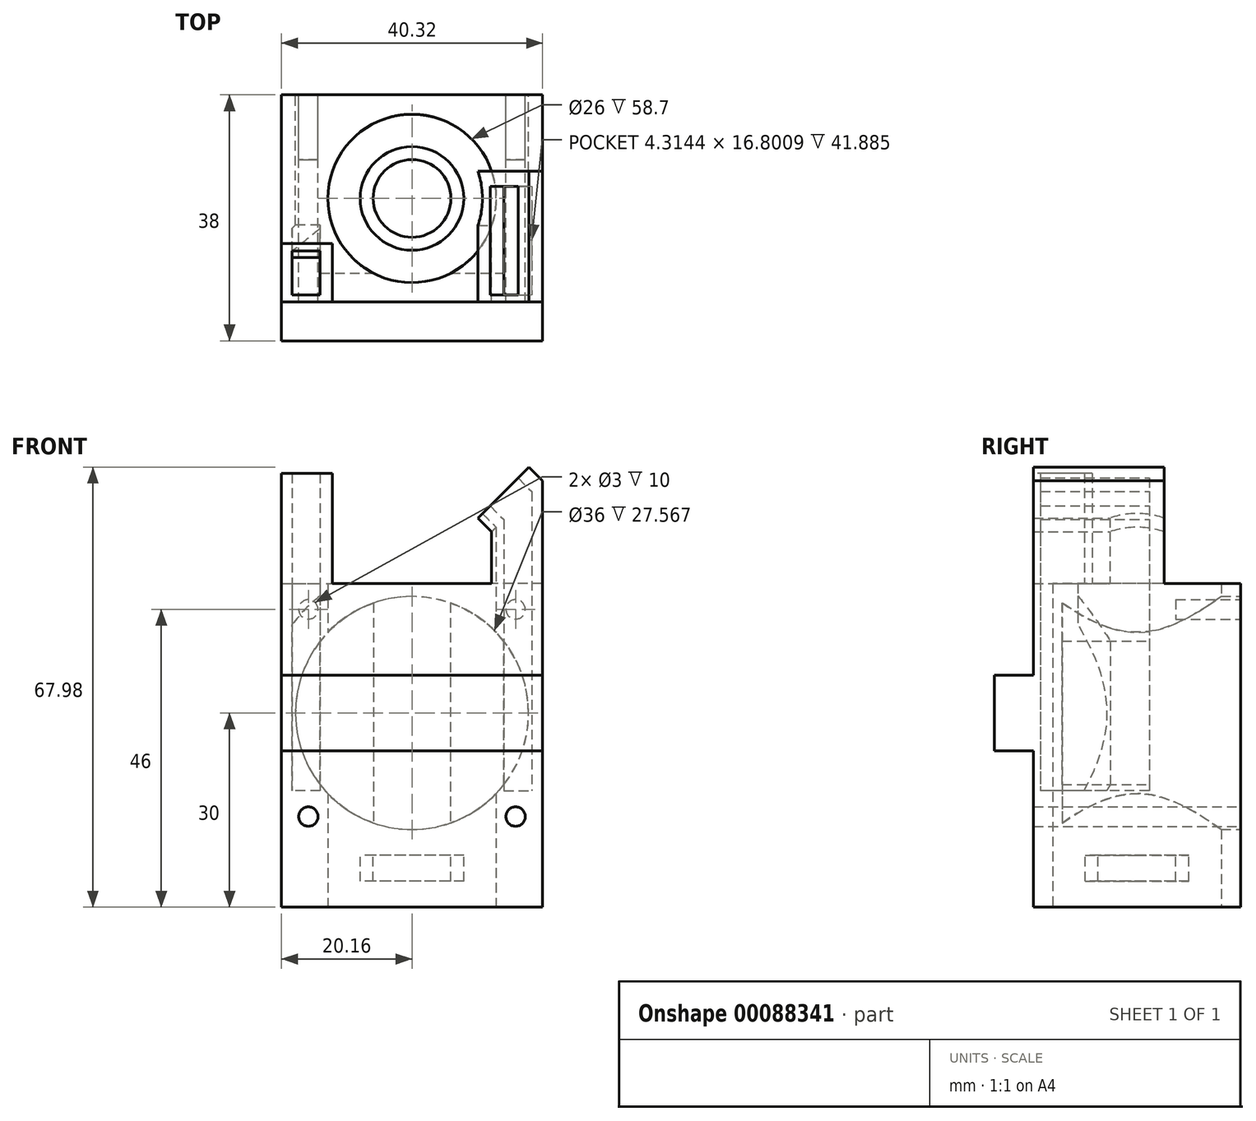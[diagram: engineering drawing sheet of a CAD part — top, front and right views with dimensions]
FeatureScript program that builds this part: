
annotation { "Feature Type Name" : "Feature", "Feature Type Description" : "" }
export const myFeature = defineFeature(function(context is Context, id is Id, definition is map)
    precondition{}
    {
        {
            var Q0;
            Q0=qCreatedBy(makeId("Top.planeOp"),FACE);
            var sketch = newSketch(context, id + "F16", { "sketchPlane" : qUnion([Q0])});
            skCircle(sketch, "E0", {"center": v(0, 0) * mm, "radius": 8 * mm});
            skCircle(sketch, "E1.cCircle", {"center": v(0, 0) * mm, "radius": 13 * mm, "construction": true});
            skLineSegment(sketch, "E1.0", {"start": v(13, 13) * mm, "end": v(13, -13) * mm});
            skLineSegment(sketch, "E1.1", {"start": v(13, -13) * mm, "end": v(-13, -13) * mm});
            skLineSegment(sketch, "E1.2", {"start": v(-13, -13) * mm, "end": v(-13, 13) * mm});
            skLineSegment(sketch, "E1.3", {"start": v(-13, 13) * mm, "end": v(13, 13) * mm});
            skPoint(sketch, "E1.0.midPoint", {"position": v(13, 0) * mm});
            skLineSegment(sketch, "E2", {"start": v(0, 0) * mm, "end": v(8, 0) * mm, "construction": true});
            skPoint(sketch, "E3.0.midPoint", {"position": v(0, 36.09) * mm});
            skLineSegment(sketch, "E4", {"start": v(0, 0) * mm, "end": v(0, -16) * mm, "construction": true});
            skPoint(sketch, "E5", {"position": v(0, -13) * mm});
            skLineSegment(sketch, "E6", {"start": v(0, -16) * mm, "end": v(20.16, -16) * mm});
            skLineSegment(sketch, "E7", {"start": v(20.16, -16) * mm, "end": v(20.16, 0) * mm});
            skLineSegment(sketch, "E8.MirrorCS", {"start": v(0, 16) * mm, "end": v(20.16, 16) * mm});
            skLineSegment(sketch, "E9.MirrorCS", {"start": v(20.16, 16) * mm, "end": v(20.16, 0) * mm});
            skLineSegment(sketch, "E10.MirrorCS", {"start": v(0, 16) * mm, "end": v(-20.16, 16) * mm});
            skLineSegment(sketch, "E11.MirrorCS", {"start": v(-20.16, 16) * mm, "end": v(-20.16, 0) * mm});
            skLineSegment(sketch, "E12.MirrorCS", {"start": v(0, -16) * mm, "end": v(-20.16, -16) * mm});
            skLineSegment(sketch, "E13.trimOffspring", {"start": v(13, 0) * mm, "end": v(20.16, 0) * mm, "construction": true});
            skPoint(sketch, "E14.middle", {"position": v(16.58, 0) * mm});
            skCircle(sketch, "E15", {"center": v(0, 0) * mm, "radius": 6 * mm});
            skCircle(sketch, "E16", {"center": v(0, 0) * mm, "radius": 13 * mm});
            skLineSegment(sketch, "E17.bottom", {"start": v(14.19, 1.9) * mm, "end": v(18.5, 1.9) * mm});
            skLineSegment(sketch, "E17.top", {"start": v(14.19, -14.9) * mm, "end": v(18.5, -14.9) * mm});
            skLineSegment(sketch, "E17.left", {"start": v(14.19, 1.9) * mm, "end": v(14.19, -14.9) * mm});
            skLineSegment(sketch, "E17.right", {"start": v(18.5, 1.9) * mm, "end": v(18.5, -14.9) * mm});
            skLineSegment(sketch, "E18.MirrorCS", {"start": v(-14.19, -14.9) * mm, "end": v(-18.5, -14.9) * mm});
            skLineSegment(sketch, "E19.MirrorCS", {"start": v(-18.5, 1.9) * mm, "end": v(-18.5, -14.9) * mm});
            skLineSegment(sketch, "E20.MirrorCS", {"start": v(-14.19, 1.9) * mm, "end": v(-18.5, 1.9) * mm});
            skLineSegment(sketch, "E21.MirrorCS", {"start": v(-14.19, 1.9) * mm, "end": v(-14.19, -14.9) * mm});
            skCircle(sketch, "E22.cCircle", {"center": v(0, 0) * mm, "radius": 12.5 * mm, "construction": true});
            skLineSegment(sketch, "E22.0", {"start": v(21.65, -12.5) * mm, "end": v(-21.65, -12.5) * mm, "construction": true});
            skPoint(sketch, "E22.0.midPoint", {"position": v(0, -12.5) * mm});
            skCircle(sketch, "E23.cCircle", {"center": v(0, 0) * mm, "radius": 9.5 * mm, "construction": true});
            skLineSegment(sketch, "E23.0", {"start": v(-16.45, 9.5) * mm, "end": v(16.45, 9.5) * mm, "construction": true});
            skLineSegment(sketch, "E23.1", {"start": v(16.45, 9.5) * mm, "end": v(0, -19) * mm, "construction": true});
            skLineSegment(sketch, "E23.2", {"start": v(0, -19) * mm, "end": v(-16.45, 9.5) * mm, "construction": true});
            skPoint(sketch, "E23.0.midPoint", {"position": v(0, 9.5) * mm});
            skCircle(sketch, "E24", {"center": v(-16.45, 9.5) * mm, "radius": 1.5 * mm});
            skCircle(sketch, "E25", {"center": v(16.45, 9.5) * mm, "radius": 1.5 * mm});
            skCircle(sketch, "E26", {"center": v(0, -19) * mm, "radius": 1.5 * mm});
            skArc(sketch, "E27", {"start": v(-13, -16) * mm, "mid": v(0, -22.28) * mm, "end": v(13, -16) * mm});
            skPoint(sketch, "E27.endSnap0", {"position": v(10.08, -16) * mm});
            skLineSegment(sketch, "E28.bottom", {"start": v(-20.16, -16) * mm, "end": v(-24.56, -16) * mm});
            skLineSegment(sketch, "E28.top", {"start": v(-20.16, 0) * mm, "end": v(-24.56, 0) * mm});
            skLineSegment(sketch, "E28.right", {"start": v(-25.56, -15) * mm, "end": v(-25.56, -1) * mm});
            skLineSegment(sketch, "E29.0", {"start": v(-20.16, -1.4) * mm, "end": v(-24.16, -1.4) * mm});
            skLineSegment(sketch, "E29.2", {"start": v(-20.16, -14.6) * mm, "end": v(-24.16, -14.6) * mm});
            skLineSegment(sketch, "E29.3", {"start": v(-24.16, -14.6) * mm, "end": v(-24.16, -1.4) * mm});
            skPoint(sketch, "E30.orphan", {"position": v(-20.16, 0) * mm});
            skLineSegment(sketch, "E31", {"start": v(-20.16, 0) * mm, "end": v(-20.16, -16) * mm});
            skPoint(sketch, "E32.visualSharp", {"position": v(-25.56, -16) * mm});
            skArc(sketch, "E32.filletArc", {"start": v(-25.56, -15) * mm, "mid": v(-25.27, -15.7) * mm, "end": v(-24.56, -16) * mm});
            skPoint(sketch, "E33.visualSharp", {"position": v(-25.56, 0) * mm});
            skArc(sketch, "E33.filletArc", {"start": v(-24.56, 0) * mm, "mid": v(-25.27, -0.3) * mm, "end": v(-25.56, -1) * mm});
            skLineSegment(sketch, "E34.MirrorCS", {"start": v(20.16, -14.6) * mm, "end": v(24.16, -14.6) * mm});
            skLineSegment(sketch, "E35.MirrorCS", {"start": v(20.16, -16) * mm, "end": v(24.56, -16) * mm});
            skLineSegment(sketch, "E36.MirrorCS", {"start": v(24.16, -14.6) * mm, "end": v(24.16, -1.4) * mm});
            skLineSegment(sketch, "E37.MirrorCS", {"start": v(25.56, -15) * mm, "end": v(25.56, -1) * mm});
            skArc(sketch, "E38.MirrorCS", {"start": v(25.56, -15) * mm, "mid": v(25.27, -15.7) * mm, "end": v(24.56, -16) * mm});
            skArc(sketch, "E39.MirrorCS", {"start": v(24.56, 0) * mm, "mid": v(25.27, -0.3) * mm, "end": v(25.56, -1) * mm});
            skLineSegment(sketch, "E40.MirrorCS", {"start": v(20.16, 0) * mm, "end": v(24.56, 0) * mm});
            skLineSegment(sketch, "E41.MirrorCS", {"start": v(20.16, -1.4) * mm, "end": v(24.16, -1.4) * mm});
            skSolve(sketch);
        }
        {
            var Q0;
            {var subQ0=sQuery(id+"F16.wireOp",EDGE,"E1.2");var subQ1=sQuery(id+"F16.wireOp",EDGE,"E1.1");var subQ2=makeQuery(id+"F16.imprint","INTERSECT",VERTEX,{"derivedFrom":[subQ1,subQ0]});Q0=makeQuery(id+"F16.imprint","IMPRINT",FACE,{"disambiguationData":[TD([[makeQuery(id+"F16.imprint","IMPRINT",EDGE,{"disambiguationData":[TD([[subQ2,1.0]])],"derivedFrom":subQ1}),-1.0]])]});}
            var Q1;
            {var subQ0=sQuery(id+"F16.wireOp",EDGE,"E1.3");var subQ1=sQuery(id+"F16.wireOp",EDGE,"E1.2");var subQ2=makeQuery(id+"F16.imprint","INTERSECT",VERTEX,{"derivedFrom":[subQ1,subQ0]});Q1=makeQuery(id+"F16.imprint","IMPRINT",FACE,{"disambiguationData":[TD([[makeQuery(id+"F16.imprint","IMPRINT",EDGE,{"disambiguationData":[TD([[subQ2,1.0]])],"derivedFrom":subQ1}),-1.0]])]});}
            var Q2;
            Q2=makeQuery(id+"F16.imprint","IMPRINT",FACE,{"disambiguationData":[TD([[makeQuery(id+"F16.imprint","IMPRINT",EDGE,{"derivedFrom":sQuery(id+"F16.wireOp",EDGE,"E6")}),1.0]])]});
            var Q3;
            {var subQ0=sQuery(id+"F16.wireOp",EDGE,"E1.1");var subQ1=sQuery(id+"F16.wireOp",EDGE,"E1.0");var subQ2=makeQuery(id+"F16.imprint","INTERSECT",VERTEX,{"derivedFrom":[subQ1,subQ0]});Q3=makeQuery(id+"F16.imprint","IMPRINT",FACE,{"disambiguationData":[TD([[makeQuery(id+"F16.imprint","IMPRINT",EDGE,{"disambiguationData":[TD([[subQ2,1.0]])],"derivedFrom":subQ1}),-1.0]])]});}
            var Q4;
            {var subQ0=sQuery(id+"F16.wireOp",EDGE,"E1.3");var subQ1=sQuery(id+"F16.wireOp",EDGE,"E1.0");var subQ2=makeQuery(id+"F16.imprint","INTERSECT",VERTEX,{"derivedFrom":[subQ1,subQ0]});Q4=makeQuery(id+"F16.imprint","IMPRINT",FACE,{"disambiguationData":[TD([[makeQuery(id+"F16.imprint","IMPRINT",EDGE,{"disambiguationData":[TD([[subQ2,-1.0]])],"derivedFrom":subQ1}),-1.0]])]});}
            var Q5;
            Q5=makeQuery(id+"F16.imprint","IMPRINT",FACE,{"disambiguationData":[TD([[makeQuery(id+"F16.imprint","IMPRINT",EDGE,{"derivedFrom":sQuery(id+"F16.wireOp",EDGE,"E24")}),1.0]])]});
            var Q6;
            Q6=makeQuery(id+"F16.imprint","IMPRINT",FACE,{"disambiguationData":[TD([[makeQuery(id+"F16.imprint","IMPRINT",EDGE,{"derivedFrom":sQuery(id+"F16.wireOp",EDGE,"E25")}),1.0]])]});
            extrude(context, id + "F0", {"entities" : qUnion([Q0, Q1, Q2, Q3, Q4, Q5, Q6]), "depth" : 32 * mm});
        }
        {
            var Q0;
            Q0=makeQuery(id+"F16.imprint","IMPRINT",FACE,{"disambiguationData":[TD([[makeQuery(id+"F16.imprint","IMPRINT",EDGE,{"derivedFrom":sQuery(id+"F16.wireOp",EDGE,"E6")}),1.0]])]});
            var Q1;
            {var subQ0=sQuery(id+"F16.wireOp",EDGE,"E1.2");var subQ1=sQuery(id+"F16.wireOp",EDGE,"E1.1");var subQ2=makeQuery(id+"F16.imprint","INTERSECT",VERTEX,{"derivedFrom":[subQ1,subQ0]});Q1=makeQuery(id+"F16.imprint","IMPRINT",FACE,{"disambiguationData":[TD([[makeQuery(id+"F16.imprint","IMPRINT",EDGE,{"disambiguationData":[TD([[subQ2,1.0]])],"derivedFrom":subQ1}),-1.0]])]});}
            var Q2;
            {var subQ0=sQuery(id+"F16.wireOp",EDGE,"E1.3");var subQ1=sQuery(id+"F16.wireOp",EDGE,"E1.2");var subQ2=makeQuery(id+"F16.imprint","INTERSECT",VERTEX,{"derivedFrom":[subQ1,subQ0]});Q2=makeQuery(id+"F16.imprint","IMPRINT",FACE,{"disambiguationData":[TD([[makeQuery(id+"F16.imprint","IMPRINT",EDGE,{"disambiguationData":[TD([[subQ2,1.0]])],"derivedFrom":subQ1}),-1.0]])]});}
            var Q3;
            {var subQ0=sQuery(id+"F16.wireOp",EDGE,"E1.3");var subQ1=sQuery(id+"F16.wireOp",EDGE,"E1.0");var subQ2=makeQuery(id+"F16.imprint","INTERSECT",VERTEX,{"derivedFrom":[subQ1,subQ0]});Q3=makeQuery(id+"F16.imprint","IMPRINT",FACE,{"disambiguationData":[TD([[makeQuery(id+"F16.imprint","IMPRINT",EDGE,{"disambiguationData":[TD([[subQ2,-1.0]])],"derivedFrom":subQ1}),-1.0]])]});}
            var Q4;
            {var subQ0=sQuery(id+"F16.wireOp",EDGE,"E1.1");var subQ1=sQuery(id+"F16.wireOp",EDGE,"E1.0");var subQ2=makeQuery(id+"F16.imprint","INTERSECT",VERTEX,{"derivedFrom":[subQ1,subQ0]});Q4=makeQuery(id+"F16.imprint","IMPRINT",FACE,{"disambiguationData":[TD([[makeQuery(id+"F16.imprint","IMPRINT",EDGE,{"disambiguationData":[TD([[subQ2,1.0]])],"derivedFrom":subQ1}),-1.0]])]});}
            var Q5;
            Q5=makeQuery(id+"F16.imprint","IMPRINT",FACE,{"disambiguationData":[TD([[makeQuery(id+"F16.imprint","IMPRINT",EDGE,{"derivedFrom":sQuery(id+"F16.wireOp",EDGE,"E14.bottom")}),-1.0]])]});
            var Q6;
            Q6=makeQuery(id+"F16.imprint","IMPRINT",FACE,{"disambiguationData":[TD([[makeQuery(id+"F16.imprint","IMPRINT",EDGE,{"derivedFrom":sQuery(id+"F16.wireOp",EDGE,"E18.MirrorCS")}),-1.0]])]});
            var Q7;
            Q7=makeQuery(id+"F16.imprint","IMPRINT",FACE,{"disambiguationData":[TD([[makeQuery(id+"F16.imprint","IMPRINT",EDGE,{"derivedFrom":sQuery(id+"F16.wireOp",EDGE,"E17.bottom")}),-1.0]])]});
            var Q8;
            Q8=makeQuery(id+"F16.imprint","IMPRINT",FACE,{"disambiguationData":[TD([[makeQuery(id+"F16.imprint","IMPRINT",EDGE,{"derivedFrom":sQuery(id+"F16.wireOp",EDGE,"E24")}),1.0]])]});
            var Q9;
            Q9=makeQuery(id+"F16.imprint","IMPRINT",FACE,{"disambiguationData":[TD([[makeQuery(id+"F16.imprint","IMPRINT",EDGE,{"derivedFrom":sQuery(id+"F16.wireOp",EDGE,"E25")}),1.0]])]});
            extrude(context, id + "F1", {"entities" : qUnion([Q0, Q1, Q2, Q3, Q4, Q5, Q6, Q7, Q8, Q9]), "operationType" : NewBodyOperationType.ADD, "oppositeDirection" : true, "depth" : 18 * mm});
        }
        {
            var Q0;
            Q0=makeQuery(id+"F16.imprint","IMPRINT",FACE,{"disambiguationData":[TD([[makeQuery(id+"F16.imprint","IMPRINT",EDGE,{"derivedFrom":sQuery(id+"F16.wireOp",EDGE,"E0")}),1.0]])]});
            extrude(context, id + "F2", {"entities" : qUnion([Q0]), "operationType" : NewBodyOperationType.ADD, "oppositeDirection" : true, "depth" : 14 * mm, "hasSecondDirection" : true, "secondDirectionOppositeDirection" : true, "secondDirectionDepth" : 10 * mm});
        }
        {
            var Q0;
            {var subQ0=sQuery(id+"F16.wireOp",EDGE,"E10.MirrorCS");var subQ1=sQuery(id+"F16.wireOp",EDGE,"E8.MirrorCS");Q0=makeQuery(id+"F1.boolean.opBoolean","MERGE",FACE,{"derivedFrom":[makeQuery(id+"F0.opExtrude","SWEPT_FACE",FACE,{"disambiguationData":[OSD([subQ1,subQ0])]}),makeQuery(id+"F1.opExtrude","SWEPT_FACE",FACE,{"disambiguationData":[OSD([subQ1,subQ0])]})]});}
            var sketch = newSketch(context, id + "F3", { "sketchPlane" : qUnion([Q0])});
            skLineSegment(sketch, "E42.bottom", {"start": v(20.16, 32) * mm, "end": v(-20.16, 32) * mm});
            skLineSegment(sketch, "E42.top", {"start": v(20.16, -8) * mm, "end": v(-20.16, -8) * mm});
            skLineSegment(sketch, "E42.left", {"start": v(20.16, 32) * mm, "end": v(20.16, -8) * mm});
            skLineSegment(sketch, "E42.right", {"start": v(-20.16, 32) * mm, "end": v(-20.16, -8) * mm});
            skLineSegment(sketch, "E43", {"start": v(0, -8) * mm, "end": v(0, 32) * mm, "construction": true});
            skCircle(sketch, "E44", {"center": v(0, 12) * mm, "radius": 18 * mm});
            skLineSegment(sketch, "E45.bottom", {"start": v(-16, -4) * mm, "end": v(16, -4) * mm, "construction": true});
            skLineSegment(sketch, "E45.top", {"start": v(-16, 28) * mm, "end": v(16, 28) * mm, "construction": true});
            skLineSegment(sketch, "E45.left", {"start": v(-16, -4) * mm, "end": v(-16, 28) * mm, "construction": true});
            skLineSegment(sketch, "E45.right", {"start": v(16, -4) * mm, "end": v(16, 28) * mm, "construction": true});
            skCircle(sketch, "E46", {"center": v(16, -4) * mm, "radius": 1.5 * mm});
            skCircle(sketch, "E47", {"center": v(-16, -4) * mm, "radius": 1.5 * mm});
            skCircle(sketch, "E48", {"center": v(-16, 28) * mm, "radius": 1.5 * mm});
            skCircle(sketch, "E49", {"center": v(16, 28) * mm, "radius": 1.5 * mm});
            skSolve(sketch);
        }
        {
            var Q0;
            Q0=makeQuery(id+"F3.imprint","IMPRINT",FACE,{"disambiguationData":[TD([[makeQuery(id+"F3.imprint","IMPRINT",EDGE,{"derivedFrom":sQuery(id+"F3.wireOp",EDGE,"E44")}),1.0]])]});
            extrude(context, id + "F4", {"entities" : qUnion([Q0]), "operationType" : NewBodyOperationType.REMOVE, "oppositeDirection" : true, "depth" : 27.57 * mm});
        }
        {
            var Q0;
            Q0=makeQuery(id+"F0.opExtrude","CAP_FACE",FACE,{"disambiguationData":[OSD([sQuery(id+"F16.wireOp",EDGE,"E6"),sQuery(id+"F16.wireOp",EDGE,"E7"),sQuery(id+"F16.wireOp",EDGE,"E8.MirrorCS"),sQuery(id+"F16.wireOp",EDGE,"E9.MirrorCS"),sQuery(id+"F16.wireOp",EDGE,"E10.MirrorCS"),sQuery(id+"F16.wireOp",EDGE,"E11.MirrorCS"),sQuery(id+"F16.wireOp",EDGE,"b87de3d7-ca0c-42f6-82a7-4077ce472d940.MirrorCS"),sQuery(id+"F16.wireOp",EDGE,"E12.MirrorCS"),sQuery(id+"F16.wireOp",EDGE,"E16"),sQuery(id+"F16.wireOp",EDGE,"E17.bottom"),sQuery(id+"F16.wireOp",EDGE,"E17.top"),sQuery(id+"F16.wireOp",EDGE,"E17.left"),sQuery(id+"F16.wireOp",EDGE,"E17.right")])],"isStart":false});
            var sketch = newSketch(context, id + "F5", { "sketchPlane" : qUnion([Q0])});
            skLineSegment(sketch, "E50", {"start": v(20.16, 4.2) * mm, "end": v(12.3, 4.2) * mm});
            skLineSegment(sketch, "E51", {"start": v(12.3, -16) * mm, "end": v(12.3, -4.2) * mm});
            skLineSegment(sketch, "E52", {"start": v(0, -16) * mm, "end": v(0, 16) * mm, "construction": true});
            skLineSegment(sketch, "E53.MirrorCS", {"start": v(-20.16, 4.2) * mm, "end": v(-12.3, 4.2) * mm});
            skLineSegment(sketch, "E54.MirrorCS", {"start": v(-12.3, -16) * mm, "end": v(-12.3, -4.2) * mm});
            skLineSegment(sketch, "E55", {"start": v(12.3, -16) * mm, "end": v(-12.3, -16) * mm});
            skLineSegment(sketch, "E56", {"start": v(-20.16, -16) * mm, "end": v(20.16, -16) * mm});
            skLineSegment(sketch, "E57", {"start": v(-18.5, 1.9) * mm, "end": v(-18.5, -8.1) * mm, "construction": true});
            skLineSegment(sketch, "E58", {"start": v(-20.16, -8.1) * mm, "end": v(-12.3, -8.1) * mm});
            skLineSegment(sketch, "E59", {"start": v(-20.16, -6.94) * mm, "end": v(-12.3, -6.94) * mm});
            skSolve(sketch);
        }
        {
            var Q0;
            {var subQ0=sQuery(id+"F5.wireOp",EDGE,"E50");Q0=makeQuery(id+"F5.imprint","IMPRINT",FACE,{"disambiguationData":[TD([[makeQuery(id+"F5.imprint","IMPRINT",EDGE,{"derivedFrom":subQ0}),1.0]])]});}
            extrude(context, id + "F6", {"entities" : qUnion([Q0]), "operationType" : NewBodyOperationType.ADD, "depth" : 18 * mm});
        }
        {
            var Q0;
            Q0=makeQuery(id+"F6.opExtrude","CAP_EDGE",EDGE,{"disambiguationData":[OSD([sQuery(id+"F5.wireOp",EDGE,"E51")])],"isStart":false});
            chamfer(context, id + "F7", {"entities" : qUnion([Q0]), "width" : 10 * mm, "tangentPropagation" : true});
        }
        {
            var Q0;
            Q0=makeQuery(id+"F7.opChamfer","BLEND_FACE",FACE,{"disambiguationData":[OSD([sQuery(id+"F5.wireOp",EDGE,"E51")])]});
            extrude(context, id + "F8", {"entities" : qUnion([Q0]), "operationType" : NewBodyOperationType.ADD, "depth" : 3 * mm});
        }
        {
            var Q0;
            {var subQ0=sQuery(id+"F5.wireOp",EDGE,"E54.MirrorCS");var subQ1=sQuery(id+"F16.wireOp",EDGE,"E12.MirrorCS");var subQ2=sQuery(id+"F16.wireOp",EDGE,"E6");var subQ3=sQuery(id+"F5.wireOp",EDGE,"E51");var subQ4=makeQuery(id+"F0.opExtrude","CAP_EDGE",EDGE,{"disambiguationData":[OSD([subQ2,subQ1])],"isStart":false});Q0=makeQuery(id+"FsD5emCuLKmZAau_1.boolean.opBoolean","MERGE",FACE,{"derivedFrom":[makeQuery(id+"F8.boolean.opBoolean","MERGE",FACE,{"derivedFrom":[makeQuery(id+"F6.boolean.opBoolean","MERGE",FACE,{"derivedFrom":[makeQuery(id+"F1.boolean.opBoolean","MERGE",FACE,{"derivedFrom":[makeQuery(id+"F0.opExtrude","SWEPT_FACE",FACE,{"disambiguationData":[OSD([subQ2,subQ1])]}),makeQuery(id+"F1.opExtrude","SWEPT_FACE",FACE,{"disambiguationData":[OSD([subQ2,subQ1])]})]}),makeQuery(id+"F6.opExtrude","SWEPT_FACE",FACE,{"disambiguationData":[OSD([subQ2,subQ1]),TDD([makeQuery(id+"F5.imprint","IMPRINT",EDGE,{"disambiguationData":[TD([[makeQuery(id+"F5.imprint","INTERSECT",VERTEX,{"derivedFrom":[subQ4,subQ3]}),1.0]])],"derivedFrom":subQ4})])]}),makeQuery(id+"F6.opExtrude","SWEPT_FACE",FACE,{"disambiguationData":[OSD([subQ2,subQ1]),TDD([makeQuery(id+"F5.imprint","IMPRINT",EDGE,{"disambiguationData":[TD([[makeQuery(id+"F5.imprint","INTERSECT",VERTEX,{"derivedFrom":[subQ4,subQ0]}),-1.0]])],"derivedFrom":subQ4})])]})]}),makeQuery(id+"F8.opExtrude","SWEPT_FACE",FACE,{"disambiguationData":[OSD([subQ2,subQ1,subQ3])]})]}),makeQuery(id+"FsD5emCuLKmZAau_1.opExtrude","SWEPT_FACE",FACE,{"disambiguationData":[OSD([subQ2,subQ1,subQ0])]})]});}
            var sketch = newSketch(context, id + "F9", { "sketchPlane" : qUnion([Q0])});
            skLineSegment(sketch, "E60.bottom", {"start": v(-19.17, 32) * mm, "end": v(20.16, 32) * mm, "construction": true});
            skLineSegment(sketch, "E60.top", {"start": v(-19.17, -8) * mm, "end": v(20.16, -8) * mm, "construction": true});
            skLineSegment(sketch, "E60.left", {"start": v(-19.17, 32) * mm, "end": v(-19.17, -8) * mm, "construction": true});
            skLineSegment(sketch, "E60.right", {"start": v(20.16, 32) * mm, "end": v(20.16, -8) * mm, "construction": true});
            skLineSegment(sketch, "E61", {"start": v(-19.17, 12) * mm, "end": v(20.16, 12) * mm, "construction": true});
            skLineSegment(sketch, "E62", {"start": v(20.16, 6.14) * mm, "end": v(-20.15, 6.14) * mm});
            skLineSegment(sketch, "E63.MirrorCS", {"start": v(20.16, 17.86) * mm, "end": v(-19.17, 17.86) * mm});
            skPoint(sketch, "E64.orphan", {"position": v(-19.17, 6.14) * mm});
            skLineSegment(sketch, "E65.bottom", {"start": v(20.16, 6.14) * mm, "end": v(-20.16, 6.14) * mm});
            skLineSegment(sketch, "E65.top", {"start": v(20.16, 17.86) * mm, "end": v(-20.16, 17.86) * mm});
            skLineSegment(sketch, "E65.left", {"start": v(20.16, 6.14) * mm, "end": v(20.16, 17.86) * mm});
            skLineSegment(sketch, "E65.right", {"start": v(-20.16, 6.14) * mm, "end": v(-20.16, 17.86) * mm});
            skSolve(sketch);
        }
        {
            var Q0;
            {var subQ7=sQuery(id+"F9.wireOp",EDGE,"E65.left");Q0=makeQuery(id+"F9.imprint","IMPRINT",FACE,{"disambiguationData":[TD([[makeQuery(id+"F9.imprint","IMPRINT",EDGE,{"derivedFrom":subQ7}),-1.0]])]});}
            extrude(context, id + "F10", {"entities" : qUnion([Q0]), "operationType" : NewBodyOperationType.ADD, "depth" : 6 * mm});
        }
        {
            var Q0;
            Q0=makeQuery(id+"F3.imprint","IMPRINT",FACE,{"disambiguationData":[TD([[makeQuery(id+"F3.imprint","IMPRINT",EDGE,{"derivedFrom":sQuery(id+"F3.wireOp",EDGE,"E46")}),1.0]])]});
            var Q1;
            Q1=makeQuery(id+"F3.imprint","IMPRINT",FACE,{"disambiguationData":[TD([[makeQuery(id+"F3.imprint","IMPRINT",EDGE,{"derivedFrom":sQuery(id+"F3.wireOp",EDGE,"E47")}),1.0]])]});
            extrude(context, id + "F11", {"entities" : qUnion([Q0, Q1]), "operationType" : NewBodyOperationType.REMOVE, "oppositeDirection" : true, "depth" : 50 * mm});
        }
        {
            var Q0;
            Q0=makeQuery(id+"F3.imprint","IMPRINT",FACE,{"disambiguationData":[TD([[makeQuery(id+"F3.imprint","IMPRINT",EDGE,{"derivedFrom":sQuery(id+"F3.wireOp",EDGE,"E48")}),1.0]])]});
            var Q1;
            Q1=makeQuery(id+"F3.imprint","IMPRINT",FACE,{"disambiguationData":[TD([[makeQuery(id+"F3.imprint","IMPRINT",EDGE,{"derivedFrom":sQuery(id+"F3.wireOp",EDGE,"E49")}),1.0]])]});
            extrude(context, id + "F12", {"entities" : qUnion([Q0, Q1]), "operationType" : NewBodyOperationType.REMOVE, "oppositeDirection" : true, "depth" : 10 * mm});
        }
        {
            var Q0;
            Q0=makeQuery(id+"F0.opExtrude","SWEPT_FACE",FACE,{"disambiguationData":[OSD([sQuery(id+"F16.wireOp",EDGE,"E20.MirrorCS")])]});
            extrude(context, id + "F13", {"entities" : qUnion([Q0]), "operationType" : NewBodyOperationType.ADD, "depth" : 11 * mm});
        }
        {
            var Q0;
            Q0=makeQuery(id+"F13.opExtrude","CAP_EDGE",EDGE,{"disambiguationData":[OSD([sQuery(id+"F16.wireOp",EDGE,"E20.MirrorCS"),sQuery(id+"F3.wireOp",EDGE,"E44")])],"isStart":false});
            chamfer(context, id + "F14", {"entities" : qUnion([Q0]), "width" : 5 * mm, "tangentPropagation" : true});
        }
        {
            var Q0;
            {var subQ0=sQuery(id+"F5.wireOp",EDGE,"E58");var subQ1=sQuery(id+"F5.wireOp",EDGE,"E54.MirrorCS");var subQ2=makeQuery(id+"F5.imprint","INTERSECT",VERTEX,{"derivedFrom":[subQ1,subQ0]});Q0=makeQuery(id+"F5.imprint","IMPRINT",FACE,{"disambiguationData":[TD([[makeQuery(id+"F5.imprint","IMPRINT",EDGE,{"disambiguationData":[TD([[subQ2,-1.0]])],"derivedFrom":subQ1}),1.0]])]});}
            var Q1;
            {var subQ0=sQuery(id+"F5.wireOp",EDGE,"E58");var subQ1=makeQuery(id+"F0.opExtrude","CAP_EDGE",EDGE,{"disambiguationData":[OSD([sQuery(id+"F16.wireOp",EDGE,"E19.MirrorCS")])],"isStart":false});var subQ2=makeQuery(id+"F5.imprint","INTERSECT",VERTEX,{"derivedFrom":[subQ1,subQ0]});Q1=makeQuery(id+"F5.imprint","IMPRINT",FACE,{"disambiguationData":[TD([[makeQuery(id+"F5.imprint","IMPRINT",EDGE,{"disambiguationData":[TD([[subQ2,-1.0]])],"derivedFrom":subQ0}),1.0]])]});}
            var Q2;
            {var subQ12=makeQuery(id+"F0.opExtrude","CAP_EDGE",EDGE,{"disambiguationData":[OSD([sQuery(id+"F16.wireOp",EDGE,"E18.MirrorCS")])],"isStart":false});Q2=makeQuery(id+"F5.imprint","IMPRINT",FACE,{"disambiguationData":[TD([[makeQuery(id+"F5.imprint","IMPRINT",EDGE,{"derivedFrom":subQ12}),1.0]])]});}
            var Q3;
            {var subQ0=sQuery(id+"F5.wireOp",EDGE,"E58");var subQ3=makeQuery(id+"F0.opExtrude","CAP_EDGE",EDGE,{"disambiguationData":[OSD([sQuery(id+"F16.wireOp",EDGE,"E19.MirrorCS")])],"isStart":false});var subQ4=makeQuery(id+"F5.imprint","INTERSECT",VERTEX,{"derivedFrom":[subQ3,subQ0]});Q3=makeQuery(id+"F5.imprint","IMPRINT",FACE,{"disambiguationData":[TD([[makeQuery(id+"F5.imprint","IMPRINT",EDGE,{"disambiguationData":[TD([[subQ4,1.0]])],"derivedFrom":subQ3}),-1.0]])]});}
            extrude(context, id + "F15", {"entities" : qUnion([Q0, Q1, Q2, Q3]), "operationType" : NewBodyOperationType.ADD, "depth" : 17 * mm});
        }
    });
